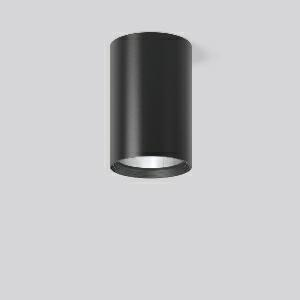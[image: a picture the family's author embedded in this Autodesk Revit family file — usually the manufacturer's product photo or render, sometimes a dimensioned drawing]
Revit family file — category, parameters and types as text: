
# Revit family: heledon_maxi_a_931225_003_3_9d5e
name_source: partatom
category: Lighting Fixtures
units: mm (PartAtom-declared; Revit-internal decimal feet)

## family parameters
Cut with Voids When Loaded = No
Host = Face
Light Source = No
Part Type = Normal
Room Calculation Point = No
Round Connector Dimension = Use Diameter
Shared = No

## types (1)
- HELEDON maxi A (1 x LED Modul 935, 4400 lm, 3500)
    Apparent Load = 35 VA
    Approval mark = CE
    CIE Flux Codes = 100 100 100 100 100
    Color Rendering = 92
    Color Temperature = 3500
    Default Elevation = 1800 mm
    Description = Series: HELEDON maxi
Cylindrical surface-mounted downlight. Housing: die-cast aluminium, powder-coated. Internal ceiling frame polycarbonate with bayonet mounting. Black plastic ring and recessed LED to prevent glare from the side. Optical assembly with reflector made of MIRO-Silver with 98% total light reflection for outstanding efficiency - can be changed without tools. Best colour rendering index Ra>90. Suitable for Ceiling mounting. Easy installation with a separate ceiling frame with bayonet mounting and plug connection. Driver integrated. Connected via plug-in connector. High quality converter without flickering and stroboscopic effect. The following accessories can be mounted without use of tools: interchangeable lenses, decorative glasses, honeycomb louvre, clear and frosted diffusers, white interchangeable plastic ring. 
Colour: deep black, matt (RAL 9005)
Diameter: 123 mm
Height: 183 mm
Lamp: LED
Socket: without socket
Colour temperature: 3500K
Colour rendering index (CRI): 92
System power: 35 W
Rated luminous flux: 4400 lm
Luminous efficiency: 126 lm/W
Control gear: Regulated power supply
Protection class: I
Type of protection: IP 20
    Height = 183 mm
    Lamp = 1 x LED Modul 935
    Lamp Light Flux = 4400 lm
    Lamp count = 1
    Length = 123 mm
    Lifetime = 50000 h
    Luminous efficacy = 126 lm/W
    Manufacturer = RZB
    ModVariant = No
    Model = 931225.003.3
    Mounting Place = Ceiling
    Mounting Type = Surface mounted
    Number of Poles = 1
    OnlyDefault = Yes
    Power Factor = 1
    Product Name = HELEDON maxi A
    Product group = Surface mounted downlights
    ProductGroupID = 302
    Protection Class = Protection class I
    Protection Degree = IP 20
    RLX_Detail_Level = 1
    RLX_Emergency_Light_Flux = 0 lm
    RLX_Emergency_Type = 0
    RLX_Emergency_Type_DB = No
    RlxData = <blob elided: 96621 chars, md5=e11960a9>
    Socket = socket
    Standby Power = 0 W
    System Light Flux = 4400 lm
    System Power = 35 W
    Type Comments = Product without accessories
    Type Image = 931192.003.jpg
    URL = http://relux.com
    VarID = ---
    Voltage = 230 V
    Voltage Range = 220-240 V
    Weight = 0.00 kg
    Width = 0 mm  [stored 0 ft]

note: [stored X ft] marks values corroborated as IEEE doubles in the binary element streams (Revit-internal decimal feet)

## geometry (parser evidence)
native form markers: Blend x4, Sweep x12
no freeform markers — native parametric forms only
